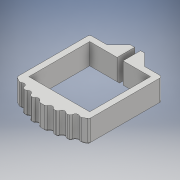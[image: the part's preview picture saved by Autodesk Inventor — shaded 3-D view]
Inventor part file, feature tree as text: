
AUTODESK INVENTOR PART (.ipt)
format: ipt  version: 2018 (Build 220112000, 112)  size: 264,704 bytes
history: native  units: mm
features: extrude x5, sketch x5, mirror x2, chamfer x2, fillet x1, projected_geometry x1
ambient origin geometry x8: Origin, YZ Plane, XZ Plane, XY Plane, X Axis, Y Axis, Z Axis, Center Point
bodies: Solid1 (feature_tree)
feature tree (16):
  extrude  "Extrusion1"  TaperAngle=135.0deg  [1 undecoded]
  extrude  "Extrusion2"  Depth=15.0mm
  extrude  "Extrusion3"  Depth=5.0mm
  mirror  "Mirror1"
  extrude  "Extrusion4"  Depth=5.0mm
  extrude  "Extrusion5"  Depth=20.0mm TaperAngle=0.0deg
  mirror  "Mirror2"
  fillet  "Fillet1"  Radius=5.0mm
  chamfer  "Chamfer2"  Distance=20.0mm
  chamfer  "Chamfer3"  Distance=12.0mm
  sketch  "Sketch2"  dims[d2=52.0mm d3=135.0deg]
  sketch  "Sketch4"  dims[d4=135.0deg d5=15.0mm]
  projected_geometry  "Projected Loop1"
  sketch  "Sketch6"  dims[d6=5.0mm d7=5.0mm]
  sketch  "Sketch7"  dims[d9=12.0mm d10=5.0mm]
  sketch  "Sketch8"  dims[d11=10.0mm d12=20.0mm d13=0.0mm d14=5.0mm d15=20.0mm d16=0.0mm d17=12.0mm d18=0.0mm d19=4.2mm d20=17.453293mm d21=10.0mm d22=0.0mm d23=5.0mm d24=9.0mm d25=9.0mm d26=9.0mm d28=10.0mm d29=0.0mm d30=2.0mm d34=2.0mm d35=2.0mm d36=45.0deg d37=2.0mm d38=2.0mm d39=45.0deg]
note: 1 required parameter value undecoded (feature->parameter linkage not recoverable at this tier; creation-order binding heuristic only, values carry confidence <= 0.55)
